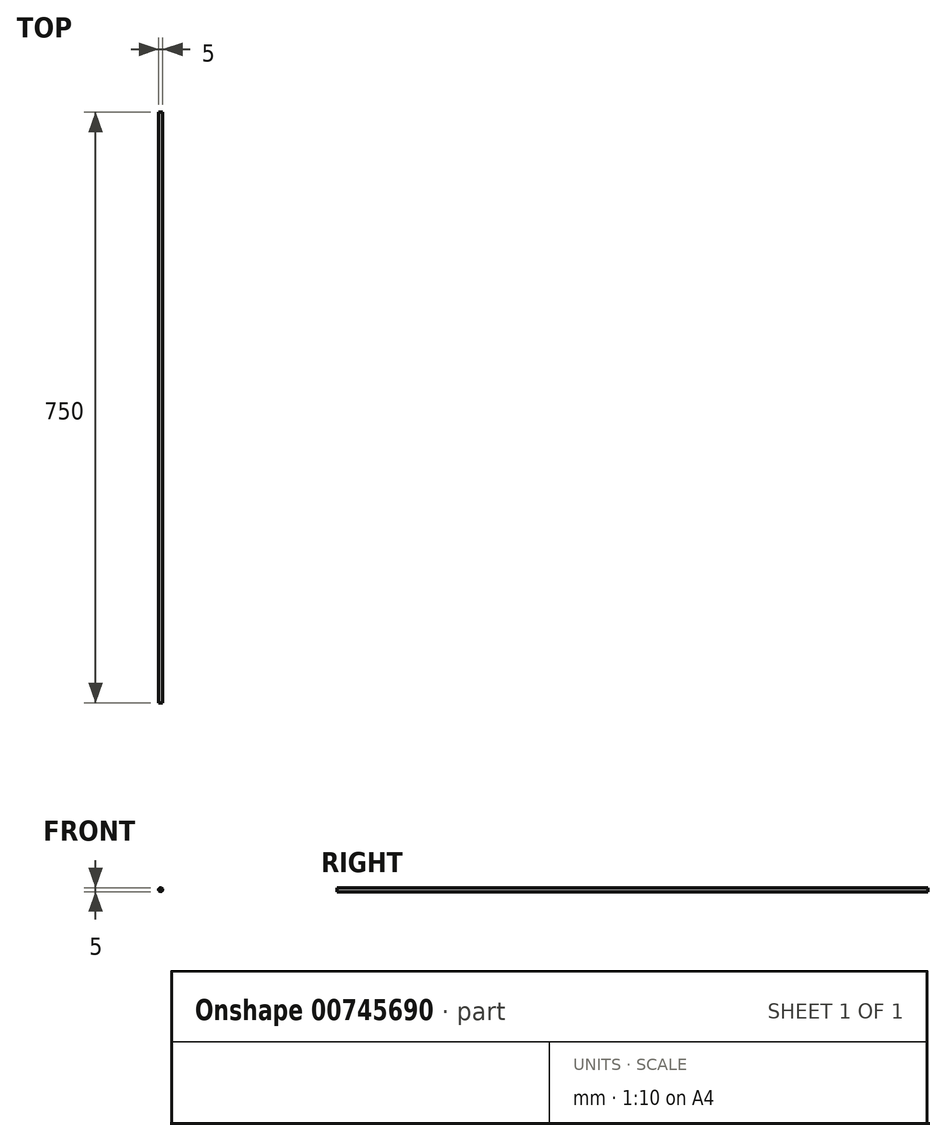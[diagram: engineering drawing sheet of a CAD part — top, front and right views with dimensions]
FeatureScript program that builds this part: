
annotation { "Feature Type Name" : "Feature", "Feature Type Description" : "" }
export const myFeature = defineFeature(function(context is Context, id is Id, definition is map)
    precondition{}
    {
        {
            var Q0;
            Q0=qCreatedBy(makeId("Front.planeOp"),FACE);
            var sketch = newSketch(context, id + "F0", { "sketchPlane" : qUnion([Q0])});
            skCircle(sketch, "E0", {"center": v(0, 0) * mm, "radius": 2.5 * mm});
            skSolve(sketch);
        }
        {
            var Q0;
            Q0 = qSketchRegion(id + "F0", true);
            extrude(context, id + "F1", {"entities" : qUnion([Q0]), "depth" : 750 * mm, "offsetDistance" : 25.4 * mm});
        }
    });
